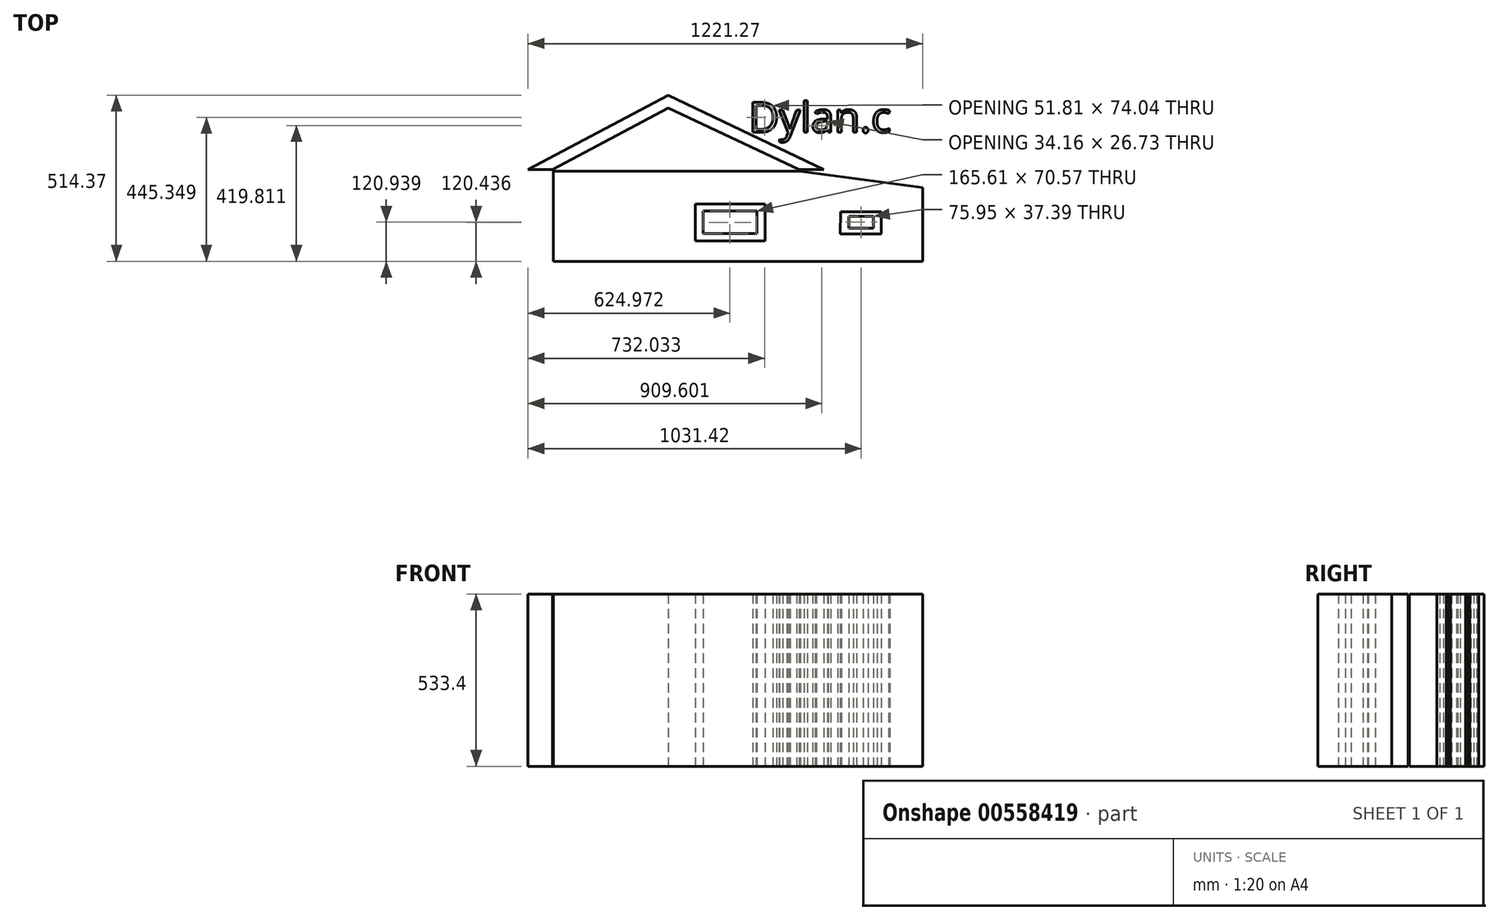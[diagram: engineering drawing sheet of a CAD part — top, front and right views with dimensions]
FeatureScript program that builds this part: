
annotation { "Feature Type Name" : "Feature", "Feature Type Description" : "" }
export const myFeature = defineFeature(function(context is Context, id is Id, definition is map)
    precondition{}
    {
        {
            var Q0;
            Q0=qCreatedBy(makeId("Top.planeOp"),FACE);
            var sketch = newSketch(context, id + "F0", { "sketchPlane" : qUnion([Q0])});
            skLineSegment(sketch, "E0", {"start": v(0, 0) * mm, "end": v(-381, 0) * mm});
            skLineSegment(sketch, "E1", {"start": v(0, 0) * mm, "end": v(0, 228.6) * mm});
            skLineSegment(sketch, "E2", {"start": v(-381, 0) * mm, "end": v(-1143, 0) * mm});
            skLineSegment(sketch, "E3", {"start": v(-381, 0) * mm, "end": v(-381, 279.4) * mm});
            skLineSegment(sketch, "E4", {"start": v(-1143, 0) * mm, "end": v(-1143, 279.4) * mm});
            skLineSegment(sketch, "E5", {"start": v(-1143, 279.4) * mm, "end": v(-381, 279.4) * mm});
            skLineSegment(sketch, "E6", {"start": v(-381, 279.4) * mm, "end": v(0, 228.6) * mm});
            skSolve(sketch);
        }
        {
            var Q0;
            Q0=makeQuery(id+"F0.imprint","IMPRINT",FACE,{"disambiguationData":[TD([[makeQuery(id+"F0.imprint","IMPRINT",EDGE,{"derivedFrom":sQuery(id+"F0.wireOp",EDGE,"E2")}),-1.0]])]});
            var sketch = newSketch(context, id + "F1", { "sketchPlane" : qUnion([Q0])});
            skLineSegment(sketch, "E7", {"start": v(-1145.07, 283.36) * mm, "end": v(-1221.27, 283.36) * mm});
            skLineSegment(sketch, "E8", {"start": v(-786.7, 283.36) * mm, "end": v(-786.7, 473.86) * mm});
            skLineSegment(sketch, "E9", {"start": v(-786.7, 473.86) * mm, "end": v(-1145.07, 283.36) * mm});
            skLineSegment(sketch, "E10", {"start": v(-381.96, 283.36) * mm, "end": v(-305.76, 283.36) * mm});
            skLineSegment(sketch, "E11", {"start": v(-381.96, 283.36) * mm, "end": v(-786.7, 473.86) * mm});
            skLineSegment(sketch, "E12", {"start": v(-1221.27, 283.36) * mm, "end": v(-786.7, 514.37) * mm});
            skLineSegment(sketch, "E13", {"start": v(-305.76, 283.36) * mm, "end": v(-786.7, 514.37) * mm});
            skLineSegment(sketch, "E14", {"start": v(-1045.46, 0) * mm, "end": v(-1045.46, 203.2) * mm});
            skLineSegment(sketch, "E15", {"start": v(-1008.66, 0) * mm, "end": v(-1008.66, 177.8) * mm});
            skLineSegment(sketch, "E16", {"start": v(-932.46, 0) * mm, "end": v(-932.46, 177.8) * mm});
            skLineSegment(sketch, "E17", {"start": v(-1008.66, 177.8) * mm, "end": v(-932.46, 177.8) * mm});
            skLineSegment(sketch, "E18", {"start": v(-1045.46, 203.2) * mm, "end": v(-899, 203.2) * mm});
            skLineSegment(sketch, "E19", {"start": v(-899, 0) * mm, "end": v(-899, 203.2) * mm});
            skSolve(sketch);
        }
        {
            var Q0;
            Q0=makeQuery(id+"F0.imprint","IMPRINT",FACE,{"disambiguationData":[TD([[makeQuery(id+"F0.imprint","IMPRINT",EDGE,{"derivedFrom":sQuery(id+"F0.wireOp",EDGE,"E2")}),-1.0]])]});
            var sketch = newSketch(context, id + "F2", { "sketchPlane" : qUnion([Q0])});
            skLineSegment(sketch, "E20", {"start": v(-651.74, 0) * mm, "end": v(-651.74, 63.5) * mm});
            skLineSegment(sketch, "E21", {"start": v(-703.59, 63.5) * mm, "end": v(-703.59, 177.8) * mm});
            skLineSegment(sketch, "E22", {"start": v(-703.59, 63.5) * mm, "end": v(-487.57, 63.5) * mm});
            skLineSegment(sketch, "E23", {"start": v(-487.57, 63.5) * mm, "end": v(-487.57, 177.8) * mm});
            skLineSegment(sketch, "E24", {"start": v(-487.57, 177.8) * mm, "end": v(-703.59, 177.8) * mm});
            skLineSegment(sketch, "E25", {"start": v(-679.1, 85.15) * mm, "end": v(-679.1, 155.72) * mm});
            skLineSegment(sketch, "E26", {"start": v(-679.1, 85.15) * mm, "end": v(-513.5, 85.15) * mm});
            skLineSegment(sketch, "E27", {"start": v(-513.5, 85.15) * mm, "end": v(-513.5, 155.72) * mm});
            skLineSegment(sketch, "E28", {"start": v(-679.1, 155.72) * mm, "end": v(-513.5, 155.72) * mm});
            skSolve(sketch);
        }
        {
            var Q0;
            Q0=makeQuery(id+"F0.imprint","IMPRINT",FACE,{"disambiguationData":[TD([[makeQuery(id+"F0.imprint","IMPRINT",EDGE,{"derivedFrom":sQuery(id+"F0.wireOp",EDGE,"E0")}),-1.0]])]});
            var sketch = newSketch(context, id + "F3", { "sketchPlane" : qUnion([Q0])});
            skLineSegment(sketch, "E29", {"start": v(-381.4, 226.45) * mm, "end": v(0, 179.36) * mm});
            skLineSegment(sketch, "E30", {"start": v(-254.7, 84.72) * mm, "end": v(-127.7, 84.72) * mm});
            skLineSegment(sketch, "E31", {"start": v(-127.7, 84.72) * mm, "end": v(-127.7, 153.65) * mm});
            skLineSegment(sketch, "E32", {"start": v(-127.7, 153.65) * mm, "end": v(-253.53, 153.65) * mm});
            skLineSegment(sketch, "E33", {"start": v(-254.7, 84.72) * mm, "end": v(-253.53, 153.65) * mm});
            skLineSegment(sketch, "E34", {"start": v(-151.87, 139.63) * mm, "end": v(-151.87, 102.24) * mm});
            skLineSegment(sketch, "E35", {"start": v(-151.87, 102.24) * mm, "end": v(-227.83, 102.24) * mm});
            skLineSegment(sketch, "E36", {"start": v(-227.83, 102.24) * mm, "end": v(-227.83, 139.63) * mm});
            skLineSegment(sketch, "E37", {"start": v(-151.87, 139.63) * mm, "end": v(-227.83, 139.63) * mm});
            skText(sketch, "E38", { "text": "Dylan.c", "fontName": "OpenSans-Regular.ttf"});
            const initialGuessF3  = {"E38": [-0.53865, 0.39902, 1, 0, 0.09347]};
            skSetInitialGuess(sketch, initialGuessF3);
            skSolve(sketch);
        }
        {
            var Q0;
            Q0 = qSketchRegion(id + "F0", true);
            var Q1;
            Q1 = qSketchRegion(id + "F1", true);
            var Q2;
            Q2 = qSketchRegion(id + "F2", true);
            var Q3;
            Q3 = qSketchRegion(id + "F3", true);
            extrude(context, id + "F4", {"entities" : qUnion([Q0, Q1, Q2, Q3]), "depth" : 25.4 * mm, "offsetDistance" : 25.4 * mm, "hasSecondDirection" : true, "secondDirectionOppositeDirection" : true, "secondDirectionDepth" : 508 * mm});
        }
    });
